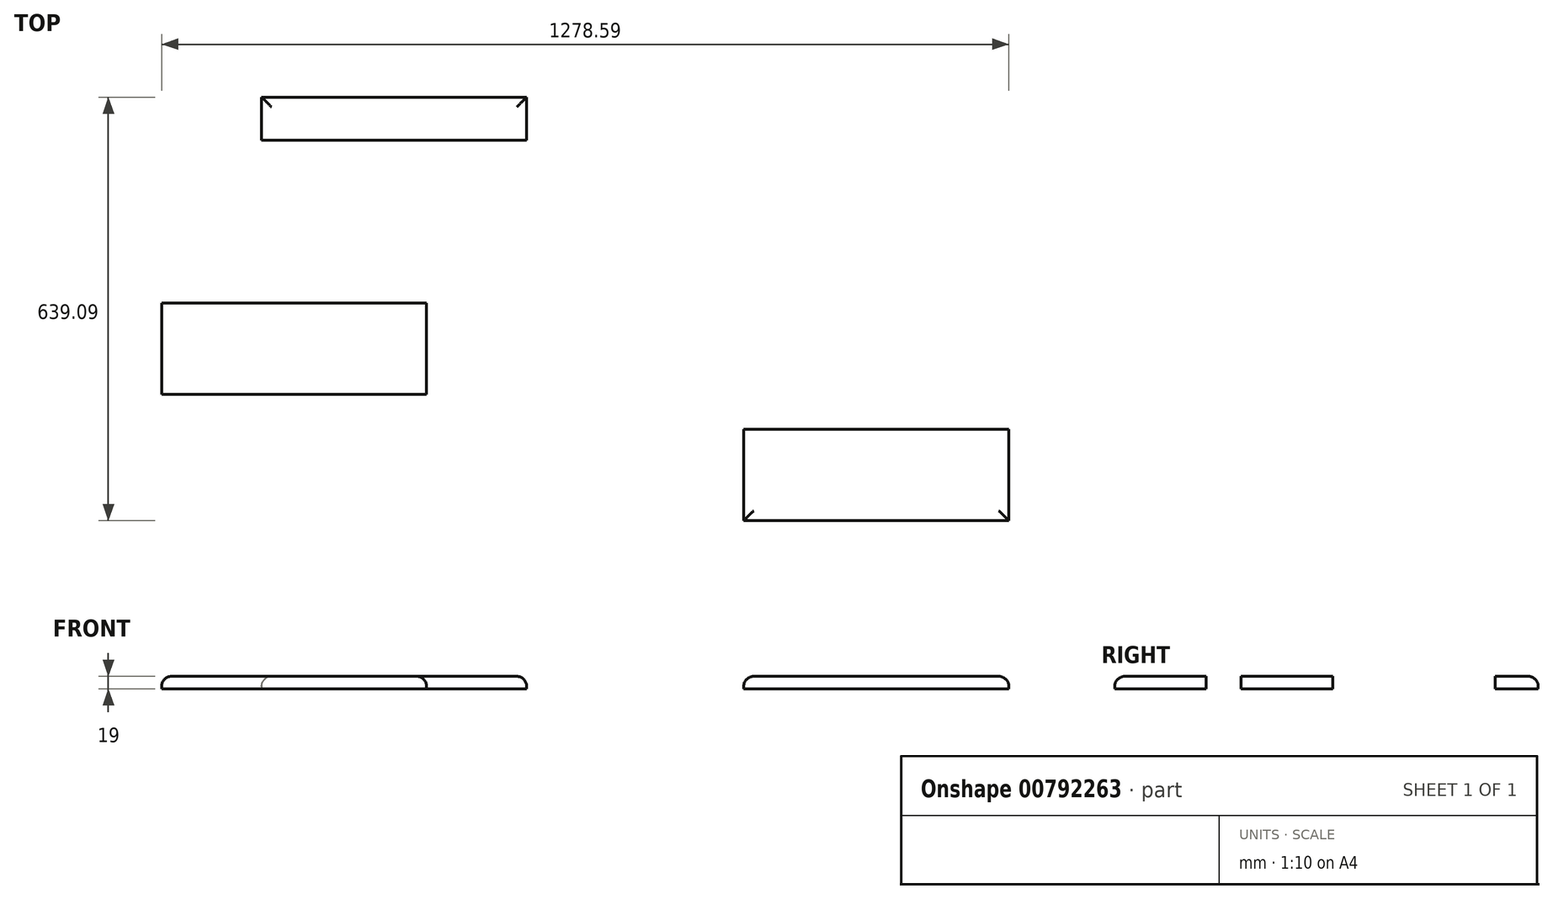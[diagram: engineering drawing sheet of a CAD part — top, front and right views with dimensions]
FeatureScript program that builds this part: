
annotation { "Feature Type Name" : "Feature", "Feature Type Description" : "" }
export const myFeature = defineFeature(function(context is Context, id is Id, definition is map)
    precondition{}
    {
        {
            var Q0;
            Q0=qCreatedBy(makeId("Top.planeOp"),FACE);
            var sketch = newSketch(context, id + "F0", { "sketchPlane" : qUnion([Q0])});
            skLineSegment(sketch, "E0.bottom", {"start": v(-228.53, 60.42) * mm, "end": v(171.47, 60.42) * mm});
            skLineSegment(sketch, "E0.top", {"start": v(-228.53, -77.58) * mm, "end": v(171.47, -77.58) * mm});
            skLineSegment(sketch, "E0.left", {"start": v(-228.53, 60.42) * mm, "end": v(-228.53, -77.58) * mm});
            skLineSegment(sketch, "E0.right", {"start": v(171.47, 60.42) * mm, "end": v(171.47, -77.58) * mm});
            skSolve(sketch);
        }
        {
            var Q0;
            Q0=qCreatedBy(makeId("Top.planeOp"),FACE);
            var sketch = newSketch(context, id + "F1", { "sketchPlane" : qUnion([Q0])});
            skLineSegment(sketch, "E1.bottom", {"start": v(-1107.12, 251.11) * mm, "end": v(-707.12, 251.11) * mm});
            skLineSegment(sketch, "E1.top", {"start": v(-1107.12, 113.11) * mm, "end": v(-707.12, 113.11) * mm});
            skLineSegment(sketch, "E1.left", {"start": v(-1107.12, 251.11) * mm, "end": v(-1107.12, 113.11) * mm});
            skLineSegment(sketch, "E1.right", {"start": v(-707.12, 251.11) * mm, "end": v(-707.12, 113.11) * mm});
            skSolve(sketch);
        }
        {
            var Q0;
            Q0=qCreatedBy(makeId("Top.planeOp"),FACE);
            var sketch = newSketch(context, id + "F2", { "sketchPlane" : qUnion([Q0])});
            skLineSegment(sketch, "E2.bottom", {"start": v(-956.1, 561.5) * mm, "end": v(-556.1, 561.5) * mm});
            skLineSegment(sketch, "E2.top", {"start": v(-956.1, 496.5) * mm, "end": v(-556.1, 496.5) * mm});
            skLineSegment(sketch, "E2.left", {"start": v(-956.1, 561.5) * mm, "end": v(-956.1, 496.5) * mm});
            skLineSegment(sketch, "E2.right", {"start": v(-556.1, 561.5) * mm, "end": v(-556.1, 496.5) * mm});
            skSolve(sketch);
        }
        {
            var Q0;
            Q0=makeQuery(id+"F2.imprint","IMPRINT",FACE,{"disambiguationData":[TD([[makeQuery(id+"F2.imprint","IMPRINT",EDGE,{"derivedFrom":sQuery(id+"F2.wireOp",EDGE,"E2.bottom")}),-1.0]])]});
            var Q1;
            Q1=makeQuery(id+"F0.imprint","IMPRINT",FACE,{"disambiguationData":[TD([[makeQuery(id+"F0.imprint","IMPRINT",EDGE,{"derivedFrom":sQuery(id+"F0.wireOp",EDGE,"E0.bottom")}),-1.0]])]});
            var Q2;
            Q2=makeQuery(id+"F1.imprint","IMPRINT",FACE,{"disambiguationData":[TD([[makeQuery(id+"F1.imprint","IMPRINT",EDGE,{"derivedFrom":sQuery(id+"F1.wireOp",EDGE,"E1.bottom")}),-1.0]])]});
            extrude(context, id + "F3", {"entities" : qUnion([Q0, Q1, Q2]), "depth" : 19 * mm, "offsetDistance" : 25 * mm});
        }
        {
            var Q0;
            Q0=makeQuery(id+"F3.opExtrude","CAP_EDGE",EDGE,{"disambiguationData":[OSD([sQuery(id+"F2.wireOp",EDGE,"E2.right")])],"isStart":false});
            var Q1;
            Q1=makeQuery(id+"F3.opExtrude","CAP_EDGE",EDGE,{"disambiguationData":[OSD([sQuery(id+"F2.wireOp",EDGE,"E2.left")])],"isStart":false});
            var Q2;
            Q2=makeQuery(id+"F3.opExtrude","CAP_EDGE",EDGE,{"disambiguationData":[OSD([sQuery(id+"F2.wireOp",EDGE,"E2.bottom")])],"isStart":false});
            var Q3;
            Q3=makeQuery(id+"F3.opExtrude","CAP_EDGE",EDGE,{"disambiguationData":[OSD([sQuery(id+"F1.wireOp",EDGE,"E1.left")])],"isStart":false});
            var Q4;
            Q4=makeQuery(id+"F3.opExtrude","CAP_EDGE",EDGE,{"disambiguationData":[OSD([sQuery(id+"F1.wireOp",EDGE,"E1.right")])],"isStart":false});
            var Q5;
            Q5=makeQuery(id+"F3.opExtrude","CAP_EDGE",EDGE,{"disambiguationData":[OSD([sQuery(id+"F0.wireOp",EDGE,"E0.left")])],"isStart":false});
            var Q6;
            Q6=makeQuery(id+"F3.opExtrude","CAP_EDGE",EDGE,{"disambiguationData":[OSD([sQuery(id+"F0.wireOp",EDGE,"E0.right")])],"isStart":false});
            var Q7;
            Q7=makeQuery(id+"F3.opExtrude","CAP_EDGE",EDGE,{"disambiguationData":[OSD([sQuery(id+"F0.wireOp",EDGE,"E0.top")])],"isStart":false});
            fillet(context, id + "F4", {"entities" : qUnion([Q0, Q1, Q2, Q3, Q4, Q5, Q6, Q7]), "radius" : 15 * mm, "tangentPropagation" : true, "allowEdgeOverflow" : false});
        }
    });
